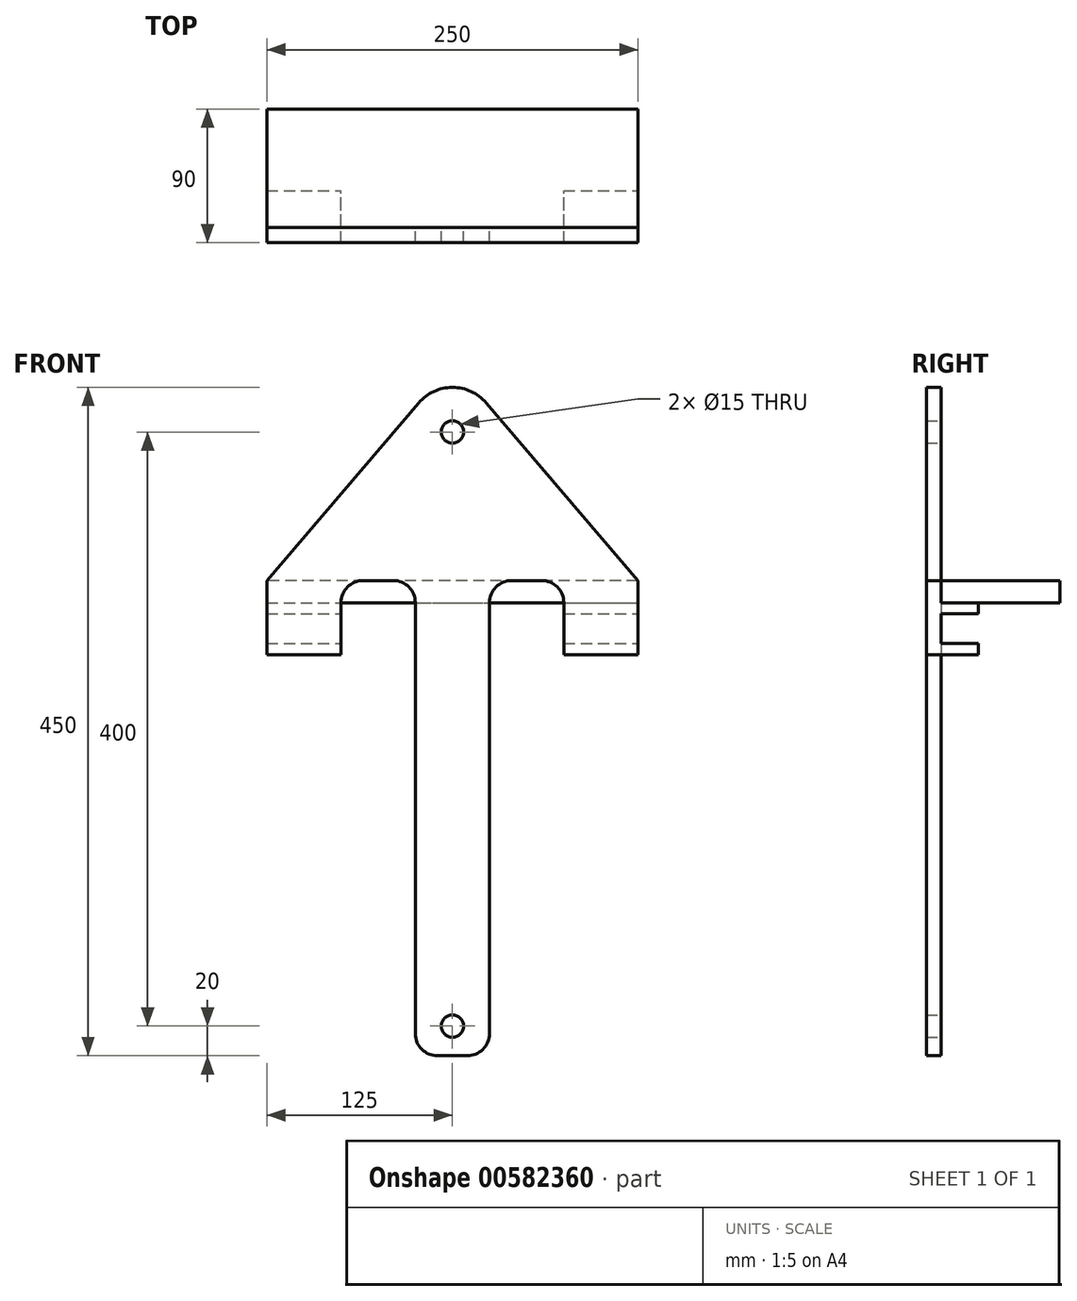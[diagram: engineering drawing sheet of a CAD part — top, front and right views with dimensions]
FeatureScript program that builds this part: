
annotation { "Feature Type Name" : "Feature", "Feature Type Description" : "" }
export const myFeature = defineFeature(function(context is Context, id is Id, definition is map)
    precondition{}
    {
        {
            var Q0;
            Q0=qCreatedBy(makeId("Front.planeOp"),FACE);
            var sketch = newSketch(context, id + "F0", { "sketchPlane" : qUnion([Q0])});
            skLineSegment(sketch, "E0", {"start": v(0, 0) * mm, "end": v(0, 150) * mm, "construction": true});
            skArc(sketch, "E1", {"start": v(22.8, 169.5) * mm, "mid": v(0, 180) * mm, "end": v(-22.8, 169.5) * mm});
            skLineSegment(sketch, "E2", {"start": v(-125, 0) * mm, "end": v(-125, 50) * mm});
            skLineSegment(sketch, "E3", {"start": v(-125, 50) * mm, "end": v(-22.8, 169.5) * mm});
            skLineSegment(sketch, "E4", {"start": v(-125, 0) * mm, "end": v(-75, 0) * mm});
            skLineSegment(sketch, "E5", {"start": v(-75, 0) * mm, "end": v(-75, 35) * mm});
            skLineSegment(sketch, "E6", {"start": v(-60, 50) * mm, "end": v(-40, 50) * mm});
            skLineSegment(sketch, "E7", {"start": v(-25, 35) * mm, "end": v(-25, -255) * mm});
            skLineSegment(sketch, "E8", {"start": v(-10, -270) * mm, "end": v(0, -270) * mm});
            skLineSegment(sketch, "E9.MirrorCS", {"start": v(10, -270) * mm, "end": v(0, -270) * mm});
            skLineSegment(sketch, "E10.MirrorCS", {"start": v(25, 35) * mm, "end": v(25, -255) * mm});
            skLineSegment(sketch, "E11.MirrorCS", {"start": v(60, 50) * mm, "end": v(40, 50) * mm});
            skLineSegment(sketch, "E12.MirrorCS", {"start": v(75, 0) * mm, "end": v(75, 35) * mm});
            skLineSegment(sketch, "E13.MirrorCS", {"start": v(125, 0) * mm, "end": v(75, 0) * mm});
            skLineSegment(sketch, "E14.MirrorCS", {"start": v(125, 0) * mm, "end": v(125, 50) * mm});
            skLineSegment(sketch, "E15.MirrorCS", {"start": v(125, 50) * mm, "end": v(22.8, 169.5) * mm});
            skCircle(sketch, "E16", {"center": v(0, 150) * mm, "radius": 7.5 * mm});
            skPoint(sketch, "E17.visualSharp", {"position": v(-75, 50) * mm});
            skArc(sketch, "E17.filletArc", {"start": v(-60, 50) * mm, "mid": v(-70.6, 45.6) * mm, "end": v(-75, 35) * mm});
            skPoint(sketch, "E18.visualSharp", {"position": v(-25, 50) * mm});
            skArc(sketch, "E18.filletArc", {"start": v(-25, 35) * mm, "mid": v(-29.4, 45.6) * mm, "end": v(-40, 50) * mm});
            skPoint(sketch, "E19.visualSharp", {"position": v(25, 50) * mm});
            skArc(sketch, "E19.filletArc", {"start": v(40, 50) * mm, "mid": v(29.4, 45.6) * mm, "end": v(25, 35) * mm});
            skPoint(sketch, "E20.visualSharp", {"position": v(75, 50) * mm});
            skArc(sketch, "E20.filletArc", {"start": v(75, 35) * mm, "mid": v(70.6, 45.6) * mm, "end": v(60, 50) * mm});
            skPoint(sketch, "E21.visualSharp", {"position": v(-25, -270) * mm});
            skArc(sketch, "E21.filletArc", {"start": v(-25, -255) * mm, "mid": v(-20.6, -265.6) * mm, "end": v(-10, -270) * mm});
            skPoint(sketch, "E22.visualSharp", {"position": v(25, -270) * mm});
            skArc(sketch, "E22.filletArc", {"start": v(10, -270) * mm, "mid": v(20.6, -265.6) * mm, "end": v(25, -255) * mm});
            skLineSegment(sketch, "E23", {"start": v(0, 0) * mm, "end": v(0, -250) * mm});
            skCircle(sketch, "E24", {"center": v(0, -250) * mm, "radius": 7.5 * mm});
            skSolve(sketch);
        }
        {
            var Q0;
            Q0=makeQuery(id+"F0.imprint","IMPRINT",FACE,{"disambiguationData":[TD([[makeQuery(id+"F0.imprint","IMPRINT",EDGE,{"derivedFrom":sQuery(id+"F0.wireOp",EDGE,"E1")}),1.0]])]});
            extrude(context, id + "F1", {"entities" : qUnion([Q0]), "depth" : 10 * mm, "offsetDistance" : 25 * mm});
        }
        {
            var Q0;
            Q0=makeQuery(id+"F1.opExtrude","CAP_FACE",FACE,{"disambiguationData":[OSD([sQuery(id+"F0.wireOp",EDGE,"E1"),sQuery(id+"F0.wireOp",EDGE,"E2"),sQuery(id+"F0.wireOp",EDGE,"E3"),sQuery(id+"F0.wireOp",EDGE,"E4"),sQuery(id+"F0.wireOp",EDGE,"E5"),sQuery(id+"F0.wireOp",EDGE,"E6"),sQuery(id+"F0.wireOp",EDGE,"E7"),sQuery(id+"F0.wireOp",EDGE,"E8"),sQuery(id+"F0.wireOp",EDGE,"E9.MirrorCS"),sQuery(id+"F0.wireOp",EDGE,"E10.MirrorCS"),sQuery(id+"F0.wireOp",EDGE,"E11.MirrorCS"),sQuery(id+"F0.wireOp",EDGE,"E12.MirrorCS"),sQuery(id+"F0.wireOp",EDGE,"E13.MirrorCS"),sQuery(id+"F0.wireOp",EDGE,"E14.MirrorCS"),sQuery(id+"F0.wireOp",EDGE,"E15.MirrorCS"),sQuery(id+"F0.wireOp",EDGE,"E16"),sQuery(id+"F0.wireOp",EDGE,"E17.filletArc"),sQuery(id+"F0.wireOp",EDGE,"E18.filletArc"),sQuery(id+"F0.wireOp",EDGE,"E19.filletArc"),sQuery(id+"F0.wireOp",EDGE,"E20.filletArc"),sQuery(id+"F0.wireOp",EDGE,"E21.filletArc"),sQuery(id+"F0.wireOp",EDGE,"E22.filletArc"),sQuery(id+"F0.wireOp",EDGE,"E24")])],"isStart":true});
            var sketch = newSketch(context, id + "F2", { "sketchPlane" : qUnion([Q0])});
            skLineSegment(sketch, "E25.bottom", {"start": v(-125, 0) * mm, "end": v(-75, 0) * mm});
            skLineSegment(sketch, "E25.top", {"start": v(-125, 35) * mm, "end": v(-75, 35) * mm});
            skLineSegment(sketch, "E25.left", {"start": v(-125, 0) * mm, "end": v(-125, 35) * mm});
            skLineSegment(sketch, "E25.right", {"start": v(-75, 0) * mm, "end": v(-75, 35) * mm});
            skLineSegment(sketch, "E26.bottom", {"start": v(125, 0) * mm, "end": v(75, 0) * mm});
            skLineSegment(sketch, "E26.top", {"start": v(125, 35) * mm, "end": v(75, 35) * mm});
            skLineSegment(sketch, "E26.left", {"start": v(125, 0) * mm, "end": v(125, 35) * mm});
            skLineSegment(sketch, "E26.right", {"start": v(75, 0) * mm, "end": v(75, 35) * mm});
            skSolve(sketch);
        }
        {
            var Q0;
            Q0 = qSketchRegion(id + "F2", true);
            extrude(context, id + "F3", {"entities" : qUnion([Q0]), "operationType" : NewBodyOperationType.ADD, "depth" : 25 * mm, "offsetDistance" : 25 * mm});
        }
        {
            var Q0;
            Q0=makeQuery(id+"F3.boolean.opBoolean","MERGE",FACE,{"derivedFrom":[makeQuery(id+"F1.opExtrude","SWEPT_FACE",FACE,{"disambiguationData":[OSD([sQuery(id+"F0.wireOp",EDGE,"E14.MirrorCS")])]}),makeQuery(id+"F3.opExtrude","SWEPT_FACE",FACE,{"disambiguationData":[OSD([sQuery(id+"F2.wireOp",EDGE,"E25.left")])]})]});
            var sketch = newSketch(context, id + "F4", { "sketchPlane" : qUnion([Q0])});
            skLineSegment(sketch, "E27.bottom", {"start": v(25, 17.5) * mm, "end": v(0, 17.5) * mm, "construction": true});
            skLineSegment(sketch, "E27.top", {"start": v(25, 27.5) * mm, "end": v(0, 27.5) * mm});
            skLineSegment(sketch, "E27.left", {"start": v(25, 17.5) * mm, "end": v(25, 27.5) * mm});
            skLineSegment(sketch, "E27.right", {"start": v(0, 17.5) * mm, "end": v(0, 27.5) * mm});
            skLineSegment(sketch, "E28.MirrorCS", {"start": v(25, 7.5) * mm, "end": v(0, 7.5) * mm});
            skLineSegment(sketch, "E29.MirrorCS", {"start": v(0, 17.5) * mm, "end": v(0, 7.5) * mm});
            skSolve(sketch);
        }
        {
            var Q0;
            Q0=makeQuery(id+"F4.imprint","IMPRINT",FACE,{"disambiguationData":[TD([[makeQuery(id+"F4.imprint","IMPRINT",EDGE,{"derivedFrom":sQuery(id+"F4.wireOp",EDGE,"E27.top")}),1.0]])]});
            var Q1;
            Q1 = qConstructionFilter(qBodyType(qCreatedBy(id + "F4" ,EDGE), BodyType.WIRE), ConstructionObject.NO);
            extrude(context, id + "F5", {"entities" : qUnion([Q0]), "operationType" : NewBodyOperationType.REMOVE, "surfaceEntities" : qUnion([Q1]), "endBound" : BoundingType.THROUGH_ALL, "oppositeDirection" : true, "depth" : 25 * mm, "offsetDistance" : 25 * mm});
        }
        {
            var Q0;
            Q0=makeQuery(id+"F1.opExtrude","CAP_FACE",FACE,{"disambiguationData":[OSD([sQuery(id+"F0.wireOp",EDGE,"E1"),sQuery(id+"F0.wireOp",EDGE,"E2"),sQuery(id+"F0.wireOp",EDGE,"E3"),sQuery(id+"F0.wireOp",EDGE,"E4"),sQuery(id+"F0.wireOp",EDGE,"E5"),sQuery(id+"F0.wireOp",EDGE,"E6"),sQuery(id+"F0.wireOp",EDGE,"E7"),sQuery(id+"F0.wireOp",EDGE,"E8"),sQuery(id+"F0.wireOp",EDGE,"E9.MirrorCS"),sQuery(id+"F0.wireOp",EDGE,"E10.MirrorCS"),sQuery(id+"F0.wireOp",EDGE,"E11.MirrorCS"),sQuery(id+"F0.wireOp",EDGE,"E12.MirrorCS"),sQuery(id+"F0.wireOp",EDGE,"E13.MirrorCS"),sQuery(id+"F0.wireOp",EDGE,"E14.MirrorCS"),sQuery(id+"F0.wireOp",EDGE,"E15.MirrorCS"),sQuery(id+"F0.wireOp",EDGE,"E16"),sQuery(id+"F0.wireOp",EDGE,"E17.filletArc"),sQuery(id+"F0.wireOp",EDGE,"E18.filletArc"),sQuery(id+"F0.wireOp",EDGE,"E19.filletArc"),sQuery(id+"F0.wireOp",EDGE,"E20.filletArc"),sQuery(id+"F0.wireOp",EDGE,"E21.filletArc"),sQuery(id+"F0.wireOp",EDGE,"E22.filletArc"),sQuery(id+"F0.wireOp",EDGE,"E24")])],"isStart":true});
            var sketch = newSketch(context, id + "F6", { "sketchPlane" : qUnion([Q0])});
            skLineSegment(sketch, "E30.bottom", {"start": v(-125, 35) * mm, "end": v(125, 35) * mm});
            skLineSegment(sketch, "E30.top", {"start": v(-125, 50) * mm, "end": v(125, 50) * mm});
            skLineSegment(sketch, "E30.left", {"start": v(-125, 35) * mm, "end": v(-125, 50) * mm});
            skLineSegment(sketch, "E30.right", {"start": v(125, 35) * mm, "end": v(125, 50) * mm});
            skSolve(sketch);
        }
        {
            var Q0;
            Q0 = qSketchRegion(id + "F6", true);
            var Q1;
            Q1 = qConstructionFilter(qBodyType(qCreatedBy(id + "F6" ,EDGE), BodyType.WIRE), ConstructionObject.NO);
            extrude(context, id + "F7", {"entities" : qUnion([Q0]), "surfaceEntities" : qUnion([Q1]), "depth" : 80 * mm, "offsetDistance" : 25 * mm});
        }
    });
